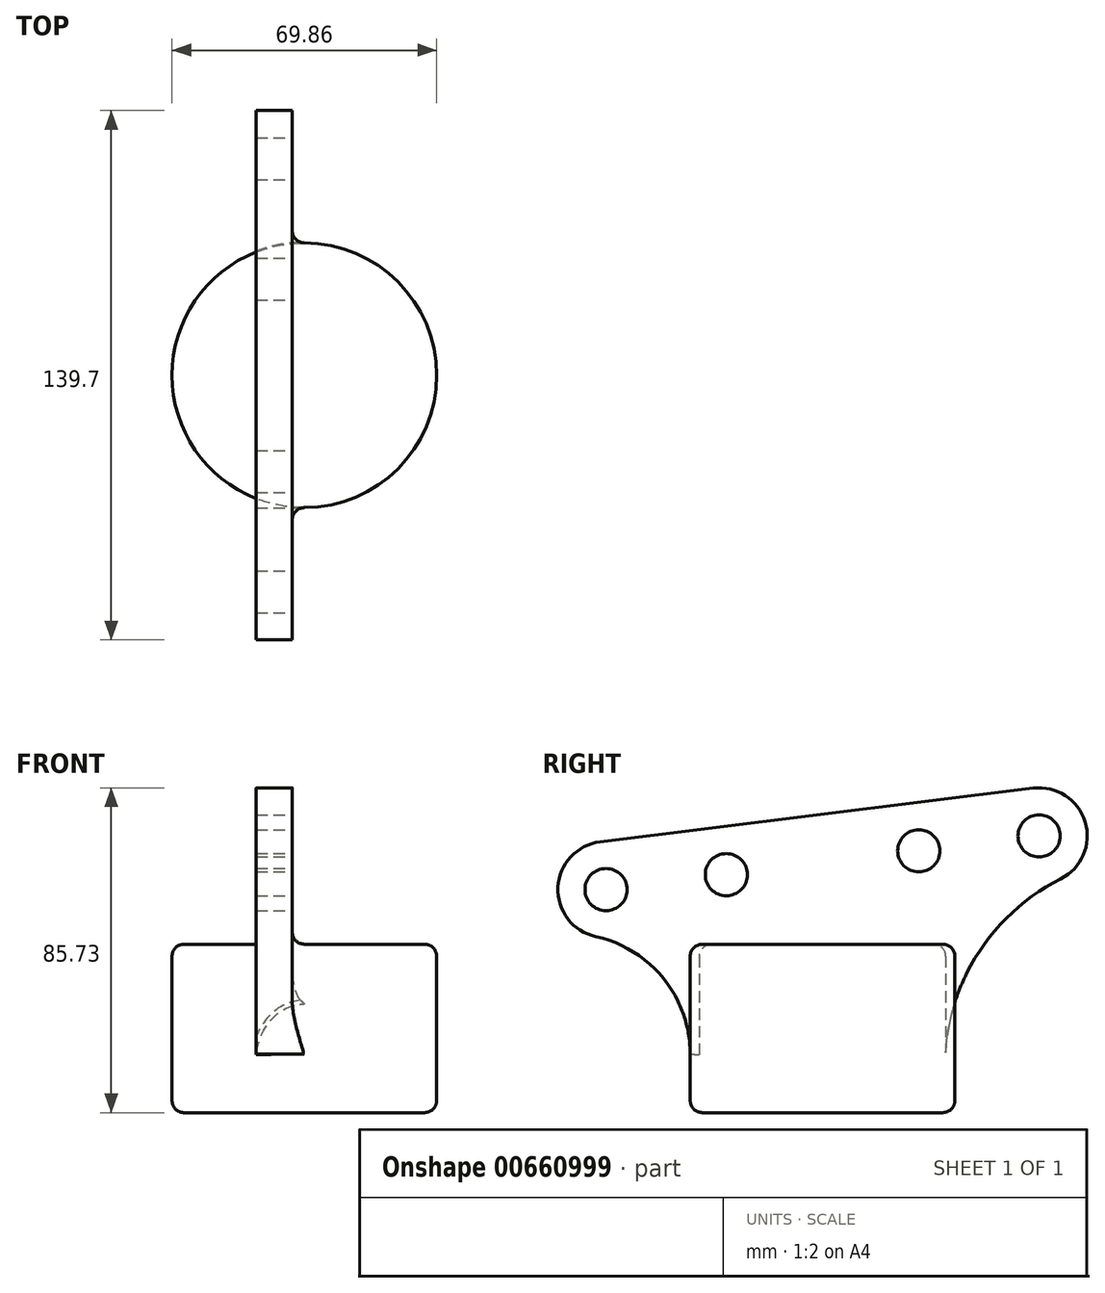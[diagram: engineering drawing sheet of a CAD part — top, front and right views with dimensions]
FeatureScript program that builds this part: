
annotation { "Feature Type Name" : "Feature", "Feature Type Description" : "" }
export const myFeature = defineFeature(function(context is Context, id is Id, definition is map)
    precondition{}
    {
        {
            var Q0;
            Q0=qCreatedBy(makeId("Front.planeOp"),FACE);
            var sketch = newSketch(context, id + "F0", { "sketchPlane" : qUnion([Q0])});
            skLineSegment(sketch, "E0", {"start": v(0, 0) * mm, "end": v(-31.75, 0) * mm});
            skLineSegment(sketch, "E1", {"start": v(-34.93, -3.18) * mm, "end": v(-34.93, -41.27) * mm});
            skLineSegment(sketch, "E2", {"start": v(-31.75, -44.45) * mm, "end": v(0, -44.45) * mm});
            skLineSegment(sketch, "E3", {"start": v(0, -44.45) * mm, "end": v(0, 0) * mm});
            skPoint(sketch, "E4.visualSharp", {"position": v(-34.93, 0) * mm});
            skArc(sketch, "E4.filletArc", {"start": v(-31.75, 0) * mm, "mid": v(-34, -0.93) * mm, "end": v(-34.93, -3.18) * mm});
            skPoint(sketch, "E5.visualSharp", {"position": v(-34.93, -44.45) * mm});
            skArc(sketch, "E5.filletArc", {"start": v(-34.92, -41.27) * mm, "mid": v(-34, -43.52) * mm, "end": v(-31.75, -44.45) * mm});
            skSolve(sketch);
        }
        {
            var Q0;
            Q0=makeQuery(id+"F0.imprint","IMPRINT",FACE,{"disambiguationData":[TD([[makeQuery(id+"F0.imprint","IMPRINT",EDGE,{"derivedFrom":sQuery(id+"F0.wireOp",EDGE,"E0")}),1.0]])]});
            var Q1;
            Q1=sQuery(id+"F0.wireOp",EDGE,"E3");
            revolve(context, id + "F1", {"entities" : qUnion([Q0]), "axis" : qUnion([Q1]), "revolveType" : RevolveType.FULL});
        }
        {
            var Q0;
            Q0=qCreatedBy(makeId("Right.planeOp"),FACE);
            cPlane(context, id + "F2", {"entities" : qUnion([Q0]), "cplaneType" : CPlaneType.OFFSET, "offset" : 3.17 * mm, "oppositeDirection" : true, "width" : 152.4 * mm, "height" : 152.4 * mm});
        }
        {
            var Q0;
            Q0=qCreatedBy(id+"F2.planeOp",FACE);
            var sketch = newSketch(context, id + "F3", { "sketchPlane" : qUnion([Q0])});
            skLineSegment(sketch, "E6", {"start": v(0, 0) * mm, "end": v(0, 28.58) * mm, "construction": true});
            skLineSegment(sketch, "E7", {"start": v(0, 28.58) * mm, "end": v(57.15, 28.58) * mm, "construction": true});
            skLineSegment(sketch, "E8", {"start": v(0, 0) * mm, "end": v(0, 14.41) * mm, "construction": true});
            skLineSegment(sketch, "E9", {"start": v(0, 14.41) * mm, "end": v(-57.15, 14.41) * mm, "construction": true});
            skArc(sketch, "E10", {"start": v(-58.71, 27.02) * mm, "mid": v(-69.84, 15) * mm, "end": v(-59.87, 2.01) * mm});
            skArc(sketch, "E11", {"start": v(62.87, 17.24) * mm, "mid": v(69.3, 32.27) * mm, "end": v(55.59, 41.18) * mm});
            skCircle(sketch, "E12", {"center": v(-57.15, 14.41) * mm, "radius": 5.56 * mm});
            skCircle(sketch, "E13", {"center": v(57.15, 28.57) * mm, "radius": 5.56 * mm});
            skLineSegment(sketch, "E14", {"start": v(-57.15, 14.41) * mm, "end": v(57.15, 28.57) * mm, "construction": true});
            skLineSegment(sketch, "E15", {"start": v(-57.15, 14.41) * mm, "end": v(-58.71, 27.02) * mm, "construction": true});
            skLineSegment(sketch, "E16", {"start": v(-58.71, 27.02) * mm, "end": v(55.59, 41.18) * mm});
            skArc(sketch, "E17", {"start": v(62.87, 17.24) * mm, "mid": v(40.45, -3.36) * mm, "end": v(32.16, -32.65) * mm});
            skArc(sketch, "E18", {"start": v(-34.93, -29) * mm, "mid": v(-41.94, -9.1) * mm, "end": v(-59.87, 2.01) * mm});
            skLineSegment(sketch, "E19", {"start": v(-34.93, -29) * mm, "end": v(32.16, -33.3) * mm});
            skLineSegment(sketch, "E20", {"start": v(32.16, -33.3) * mm, "end": v(32.16, -32.65) * mm});
            skLineSegment(sketch, "E21", {"start": v(0, 0) * mm, "end": v(25.4, 0) * mm, "construction": true});
            skLineSegment(sketch, "E22", {"start": v(25.4, 0) * mm, "end": v(25.4, 24.64) * mm, "construction": true});
            skLineSegment(sketch, "E23", {"start": v(0, 0) * mm, "end": v(-25.4, 0) * mm, "construction": true});
            skLineSegment(sketch, "E24", {"start": v(-25.4, 0) * mm, "end": v(-25.4, 18.35) * mm, "construction": true});
            skCircle(sketch, "E25", {"center": v(-25.4, 18.35) * mm, "radius": 5.56 * mm});
            skCircle(sketch, "E26", {"center": v(25.4, 24.64) * mm, "radius": 5.56 * mm});
            skSolve(sketch);
        }
        {
            var Q0;
            Q0=makeQuery(id+"F3.imprint","IMPRINT",FACE,{"disambiguationData":[TD([[makeQuery(id+"F3.imprint","IMPRINT",EDGE,{"derivedFrom":sQuery(id+"F3.wireOp",EDGE,"E10")}),1.0]])]});
            extrude(context, id + "F4", {"entities" : qUnion([Q0]), "operationType" : NewBodyOperationType.ADD, "oppositeDirection" : true, "depth" : 9.52 * mm, "offsetDistance" : 25.4 * mm});
        }
        {
            var Q0;
            Q0=makeQuery(id+"F4.boolean.opBoolean","INTERSECT",EDGE,{"disambiguationData":[OD(0.0)],"derivedFrom":[makeQuery(id+"F1.opRevolve","SWEPT_FACE",FACE,{"disambiguationData":[OSD([sQuery(id+"F0.wireOp",EDGE,"E1")])]}),makeQuery(id+"F4.opExtrude","CAP_FACE",FACE,{"disambiguationData":[OSD([sQuery(id+"F3.wireOp",EDGE,"E10"),sQuery(id+"F3.wireOp",EDGE,"E11"),sQuery(id+"F3.wireOp",EDGE,"E12"),sQuery(id+"F3.wireOp",EDGE,"E13"),sQuery(id+"F3.wireOp",EDGE,"E16"),sQuery(id+"F3.wireOp",EDGE,"E17"),sQuery(id+"F3.wireOp",EDGE,"E18"),sQuery(id+"F3.wireOp",EDGE,"E19"),sQuery(id+"F3.wireOp",EDGE,"E20")])],"isStart":true})]});
            var Q1;
            Q1=makeQuery(id+"F4.boolean.opBoolean","INTERSECT",EDGE,{"derivedFrom":[makeQuery(id+"F1.opRevolve","SWEPT_FACE",FACE,{"disambiguationData":[OSD([sQuery(id+"F0.wireOp",EDGE,"E1")])]}),makeQuery(id+"F4.opExtrude","SWEPT_FACE",FACE,{"disambiguationData":[OSD([sQuery(id+"F3.wireOp",EDGE,"E17")])]})]});
            fillet(context, id + "F5", {"entities" : qUnion([Q0, Q1]), "radius" : 3.17 * mm, "tangentPropagation" : true, "allowEdgeOverflow" : false});
        }
    });
